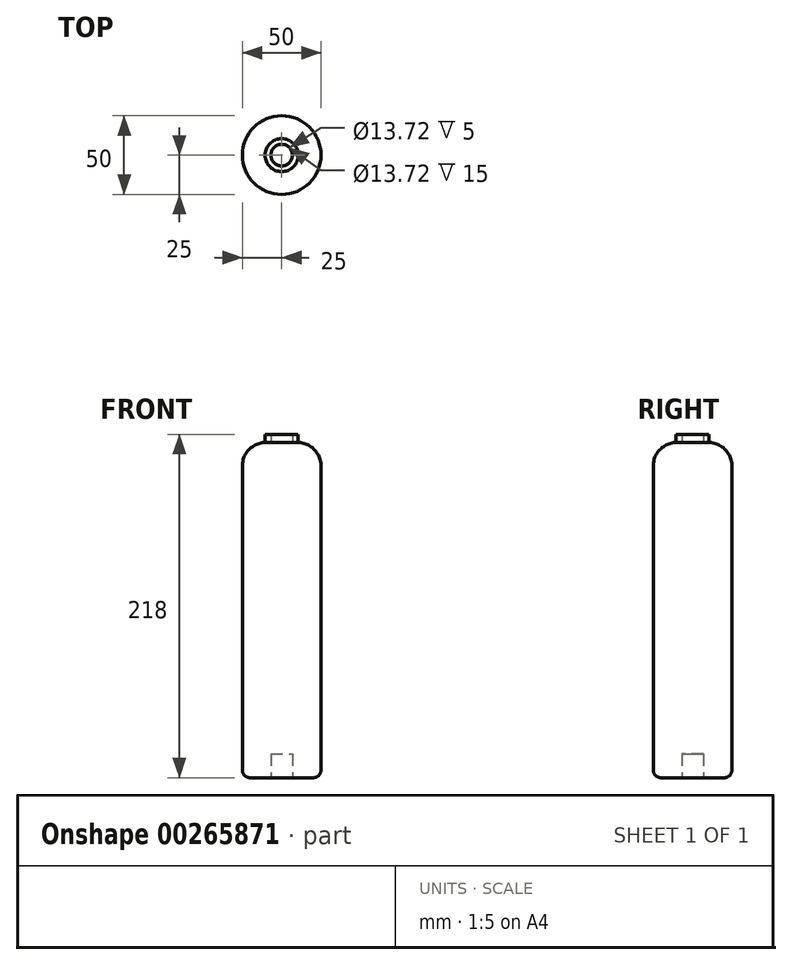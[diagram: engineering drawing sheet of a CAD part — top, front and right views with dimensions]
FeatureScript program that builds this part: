
annotation { "Feature Type Name" : "Feature", "Feature Type Description" : "" }
export const myFeature = defineFeature(function(context is Context, id is Id, definition is map)
    precondition{}
    {
        {
            var Q0;
            Q0=qCreatedBy(makeId("Top.planeOp"),FACE);
            var sketch = newSketch(context, id + "F0", { "sketchPlane" : qUnion([Q0])});
            skCircle(sketch, "E0", {"center": v(0, 0) * mm, "radius": 25 * mm});
            skSolve(sketch);
        }
        {
            var Q0;
            Q0=makeQuery(id+"F0.imprint","IMPRINT",FACE,{"disambiguationData":[TD([[makeQuery(id+"F0.imprint","IMPRINT",EDGE,{"derivedFrom":sQuery(id+"F0.wireOp",EDGE,"E0")}),1.0]])]});
            extrude(context, id + "F1", {"entities" : qUnion([Q0]), "depth" : 213 * mm, "offsetDistance" : 25 * mm});
        }
        {
            var Q0;
            Q0=makeQuery(id+"F1.opExtrude","CAP_EDGE",EDGE,{"disambiguationData":[OSD([sQuery(id+"F0.wireOp",EDGE,"E0")])],"isStart":false});
            fillet(context, id + "F2", {"entities" : qUnion([Q0]), "tangentPropagation" : true, "radius" : 15 * mm, "defaultsChanged" : true, "vertexSettings" : [], "allowEdgeOverflow" : false});
        }
        {
            var Q0;
            Q0=makeQuery(id+"F1.opExtrude","CAP_EDGE",EDGE,{"disambiguationData":[OSD([sQuery(id+"F0.wireOp",EDGE,"E0")])],"isStart":true});
            fillet(context, id + "F3", {"entities" : qUnion([Q0]), "tangentPropagation" : true, "radius" : 5 * mm, "defaultsChanged" : false, "vertexSettings" : [], "allowEdgeOverflow" : false});
        }
        {
            var Q0;
            Q0=makeQuery(id+"F1.opExtrude","CAP_FACE",FACE,{"disambiguationData":[OSD([sQuery(id+"F0.wireOp",EDGE,"E0")])],"isStart":false});
            var sketch = newSketch(context, id + "F4", { "sketchPlane" : qUnion([Q0])});
            skCircle(sketch, "E1", {"center": v(0, 0) * mm, "radius": 10.5 * mm});
            skCircle(sketch, "E2", {"center": v(0, 0) * mm, "radius": 6.86 * mm});
            skSolve(sketch);
        }
        {
            var Q0;
            Q0 = qSketchRegion(id + "F4", true);
            extrude(context, id + "F5", {"entities" : qUnion([Q0]), "depth" : 5 * mm, "offsetDistance" : 25 * mm});
        }
        {
            var Q0;
            Q0=makeQuery(id+"F1.opExtrude","CAP_FACE",FACE,{"disambiguationData":[OSD([sQuery(id+"F0.wireOp",EDGE,"E0")])],"isStart":true});
            var sketch = newSketch(context, id + "F6", { "sketchPlane" : qUnion([Q0])});
            skCircle(sketch, "E3", {"center": v(0, 0) * mm, "radius": 6.86 * mm});
            skSolve(sketch);
        }
        {
            var Q0;
            Q0=makeQuery(id+"F6.imprint","IMPRINT",FACE,{"disambiguationData":[TD([[makeQuery(id+"F6.imprint","IMPRINT",EDGE,{"derivedFrom":sQuery(id+"F6.wireOp",EDGE,"E3")}),1.0]])]});
            extrude(context, id + "F7", {"entities" : qUnion([Q0]), "operationType" : NewBodyOperationType.REMOVE, "oppositeDirection" : true, "depth" : 15 * mm, "offsetDistance" : 25 * mm});
        }
    });
